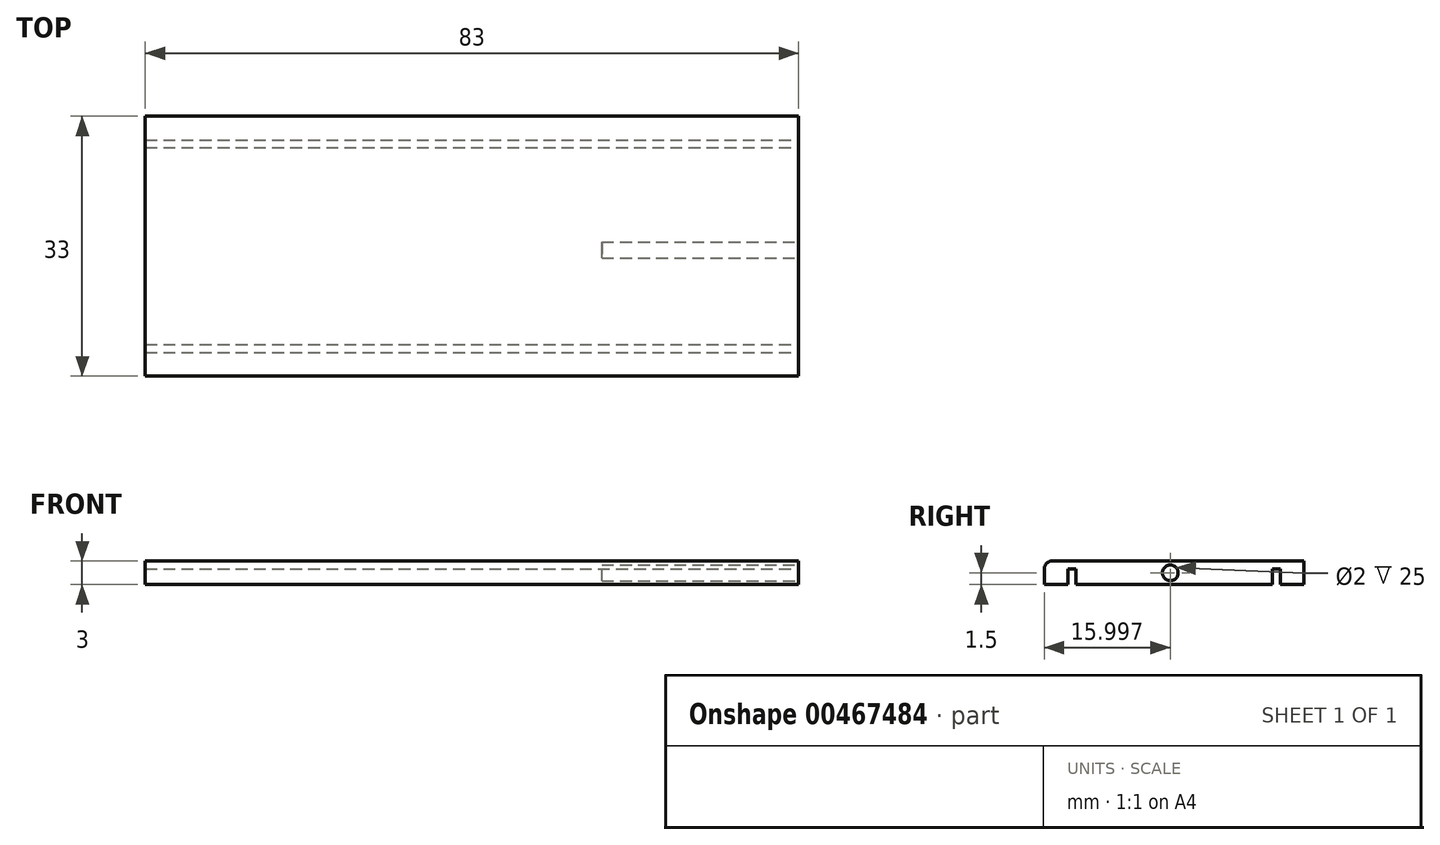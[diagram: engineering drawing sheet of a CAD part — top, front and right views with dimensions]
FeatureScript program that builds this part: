
annotation { "Feature Type Name" : "Feature", "Feature Type Description" : "" }
export const myFeature = defineFeature(function(context is Context, id is Id, definition is map)
    precondition{}
    {
        {
            var Q0;
            Q0=qCreatedBy(makeId("Top.planeOp"),FACE);
            var sketch = newSketch(context, id + "F0", { "sketchPlane" : qUnion([Q0])});
            skLineSegment(sketch, "E0.bottom", {"start": v(-61.04, 0.79) * mm, "end": v(21.96, 0.79) * mm});
            skLineSegment(sketch, "E0.top", {"start": v(-61.04, -32.21) * mm, "end": v(21.96, -32.21) * mm});
            skLineSegment(sketch, "E0.left", {"start": v(-61.04, 0.79) * mm, "end": v(-61.04, -32.21) * mm});
            skLineSegment(sketch, "E0.right", {"start": v(21.96, 0.79) * mm, "end": v(21.96, -32.21) * mm});
            skSolve(sketch);
        }
        {
            var Q0;
            Q0 = qSketchRegion(id + "F0", true);
            extrude(context, id + "F1", {"entities" : qUnion([Q0]), "depth" : 3 * mm});
        }
        {
            var Q0;
            Q0=makeQuery(id+"F1.opExtrude","SWEPT_FACE",FACE,{"disambiguationData":[OSD([sQuery(id+"F0.wireOp",EDGE,"E0.right")])]});
            var sketch = newSketch(context, id + "F2", { "sketchPlane" : qUnion([Q0])});
            skLineSegment(sketch, "E1.bottom", {"start": v(-29.21, 0) * mm, "end": v(-28.21, 0) * mm});
            skLineSegment(sketch, "E1.top", {"start": v(-29.21, 2) * mm, "end": v(-28.21, 2) * mm});
            skLineSegment(sketch, "E1.left", {"start": v(-29.21, 0) * mm, "end": v(-29.21, 2) * mm});
            skLineSegment(sketch, "E1.right", {"start": v(-28.21, 0) * mm, "end": v(-28.21, 2) * mm});
            skLineSegment(sketch, "E2.bottom", {"start": v(-3.21, 0) * mm, "end": v(-2.21, 0) * mm});
            skLineSegment(sketch, "E2.top", {"start": v(-3.21, 2) * mm, "end": v(-2.21, 2) * mm});
            skLineSegment(sketch, "E2.left", {"start": v(-3.21, 0) * mm, "end": v(-3.21, 2) * mm});
            skLineSegment(sketch, "E2.right", {"start": v(-2.21, 0) * mm, "end": v(-2.21, 2) * mm});
            skSolve(sketch);
        }
        {
            var Q0;
            Q0 = qSketchRegion(id + "F2", true);
            extrude(context, id + "F3", {"entities" : qUnion([Q0]), "operationType" : NewBodyOperationType.REMOVE, "endBound" : BoundingType.THROUGH_ALL, "oppositeDirection" : true, "depth" : 25 * mm});
        }
        {
            var Q0;
            {var subQ0=sQuery(id+"F0.wireOp",EDGE,"E0.left");var subQ1=sQuery(id+"F0.wireOp",EDGE,"E0.right");Q0=makeQuery(id+"F3.boolean.opBoolean","SPLIT",FACE,{"disambiguationData":[TD([makeQuery(id+"F3.opExtrude","SWEPT_FACE",FACE,{"disambiguationData":[OSD([sQuery(id+"F2.wireOp",EDGE,"E1.right")])]})])],"derivedFrom":makeQuery(id+"F1.opExtrude","CAP_FACE",FACE,{"disambiguationData":[OSD([sQuery(id+"F0.wireOp",EDGE,"E0.bottom"),sQuery(id+"F0.wireOp",EDGE,"E0.top"),subQ0,subQ1])],"isStart":true})});}
            var sketch = newSketch(context, id + "F4", { "sketchPlane" : qUnion([Q0])});
            skLineSegment(sketch, "E3.bottom", {"start": v(-46.56, 28.21) * mm, "end": v(-43.57, 28.21) * mm});
            skLineSegment(sketch, "E3.top", {"start": v(-46.56, 3.21) * mm, "end": v(-43.57, 3.21) * mm});
            skLineSegment(sketch, "E3.left", {"start": v(-46.56, 28.21) * mm, "end": v(-46.56, 3.21) * mm});
            skLineSegment(sketch, "E3.right", {"start": v(-43.57, 28.21) * mm, "end": v(-43.57, 3.21) * mm});
            skSolve(sketch);
        }
        {
            var Q0;
            Q0 = qSketchRegion(id + "F4", true);
            extrude(context, id + "F5", {"entities" : qUnion([Q0]), "operationType" : NewBodyOperationType.ADD, "oppositeDirection" : true, "depth" : 2 * mm});
        }
        {
            var Q0;
            Q0=makeQuery(id+"F1.opExtrude","SWEPT_FACE",FACE,{"disambiguationData":[OSD([sQuery(id+"F0.wireOp",EDGE,"E0.right")])]});
            var sketch = newSketch(context, id + "F6", { "sketchPlane" : qUnion([Q0])});
            skCircle(sketch, "E4", {"center": v(-16.21, 1.5) * mm, "radius": 1 * mm});
            skSolve(sketch);
        }
        {
            var Q0;
            Q0 = qSketchRegion(id + "F6", true);
            extrude(context, id + "F7", {"entities" : qUnion([Q0]), "operationType" : NewBodyOperationType.REMOVE, "oppositeDirection" : true, "depth" : 25 * mm, "offsetDistance" : 25 * mm});
        }
        {
            var Q0;
            Q0=makeQuery(id+"F1.opExtrude","CAP_EDGE",EDGE,{"disambiguationData":[OSD([sQuery(id+"F0.wireOp",EDGE,"E0.top")])],"isStart":false});
            fillet(context, id + "F8", {"entities" : qUnion([Q0]), "radius" : 1 * mm, "tangentPropagation" : true, "allowEdgeOverflow" : false});
        }
    });
